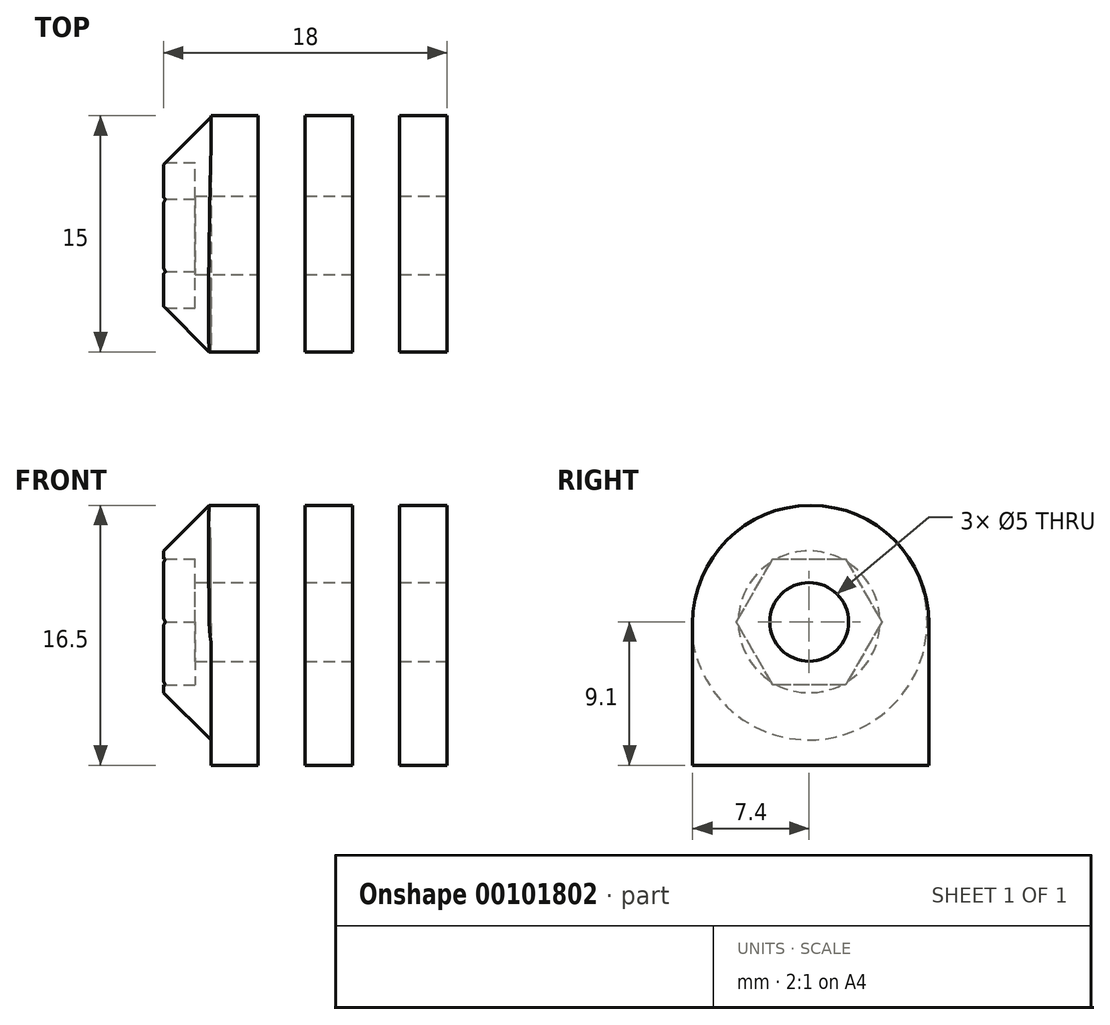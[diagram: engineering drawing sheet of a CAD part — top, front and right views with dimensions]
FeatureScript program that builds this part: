
annotation { "Feature Type Name" : "Feature", "Feature Type Description" : "" }
export const myFeature = defineFeature(function(context is Context, id is Id, definition is map)
    precondition{}
    {
        {
            var Q0;
            Q0=qCreatedBy(makeId("Top.planeOp"),FACE);
            var sketch = newSketch(context, id + "F0", { "sketchPlane" : qUnion([Q0])});
            skLineSegment(sketch, "E0.bottom", {"start": v(0, 15) * mm, "end": v(3, 15) * mm});
            skLineSegment(sketch, "E0.top", {"start": v(0, 0) * mm, "end": v(3, 0) * mm});
            skLineSegment(sketch, "E0.left", {"start": v(0, 15) * mm, "end": v(0, 0) * mm});
            skLineSegment(sketch, "E0.right", {"start": v(3, 15) * mm, "end": v(3, 0) * mm});
            skLineSegment(sketch, "E1.1.0.0", {"start": v(9, 15) * mm, "end": v(9, 0) * mm});
            skLineSegment(sketch, "E1.1.0.1", {"start": v(6, 15) * mm, "end": v(9, 15) * mm});
            skLineSegment(sketch, "E1.1.0.2", {"start": v(6, 15) * mm, "end": v(6, 0) * mm});
            skLineSegment(sketch, "E1.1.0.3", {"start": v(6, 0) * mm, "end": v(9, 0) * mm});
            skLineSegment(sketch, "E1.2.0.0", {"start": v(15, 15) * mm, "end": v(15, 0) * mm});
            skLineSegment(sketch, "E1.2.0.1", {"start": v(12, 15) * mm, "end": v(15, 15) * mm});
            skLineSegment(sketch, "E1.2.0.2", {"start": v(12, 15) * mm, "end": v(12, 0) * mm});
            skLineSegment(sketch, "E1.2.0.3", {"start": v(12, 0) * mm, "end": v(15, 0) * mm});
            skLineSegment(sketch, "E1.direction1", {"start": v(3, 0) * mm, "end": v(9, 0) * mm, "construction": true});
            skSolve(sketch);
        }
        {
            var Q0;
            Q0 = qSketchRegion(id + "F0", true);
            extrude(context, id + "F1", {"entities" : qUnion([Q0]), "depth" : 16.5 * mm});
        }
        {
            var Q0;
            Q0=qCreatedBy(makeId("Right.planeOp"),FACE);
            var sketch = newSketch(context, id + "F2", { "sketchPlane" : qUnion([Q0])});
            skCircle(sketch, "E2", {"center": v(7.4, 9.1) * mm, "radius": 2.5 * mm});
            skCircle(sketch, "E3.cCircle", {"center": v(7.4, 9.1) * mm, "radius": 4 * mm, "construction": true});
            skLineSegment(sketch, "E3.0", {"start": v(5.1, 13.1) * mm, "end": v(9.7, 13.1) * mm});
            skLineSegment(sketch, "E3.1", {"start": v(9.7, 13.1) * mm, "end": v(12.02, 9.1) * mm});
            skLineSegment(sketch, "E3.2", {"start": v(12.02, 9.1) * mm, "end": v(9.7, 5.1) * mm});
            skLineSegment(sketch, "E3.3", {"start": v(9.7, 5.1) * mm, "end": v(5.1, 5.1) * mm});
            skLineSegment(sketch, "E3.4", {"start": v(5.1, 5.1) * mm, "end": v(2.78, 9.1) * mm});
            skLineSegment(sketch, "E3.5", {"start": v(2.78, 9.1) * mm, "end": v(5.1, 13.1) * mm});
            skPoint(sketch, "E3.0.midPoint", {"position": v(7.4, 13.1) * mm});
            skCircle(sketch, "E4", {"center": v(7.4, 9.1) * mm, "radius": 5.5 * mm});
            skSolve(sketch);
        }
        {
            var Q0;
            Q0=makeQuery(id+"F2.imprint","IMPRINT",FACE,{"disambiguationData":[TD([[makeQuery(id+"F2.imprint","IMPRINT",EDGE,{"derivedFrom":sQuery(id+"F2.wireOp",EDGE,"E3.0")}),1.0]])]});
            extrude(context, id + "F3", {"entities" : qUnion([Q0]), "operationType" : NewBodyOperationType.ADD, "oppositeDirection" : true, "depth" : 3 * mm});
        }
        {
            var Q0;
            Q0=makeQuery(id+"F2.imprint","IMPRINT",FACE,{"disambiguationData":[TD([[makeQuery(id+"F2.imprint","IMPRINT",EDGE,{"derivedFrom":sQuery(id+"F2.wireOp",EDGE,"E2")}),1.0]])]});
            extrude(context, id + "F4", {"entities" : qUnion([Q0]), "operationType" : NewBodyOperationType.REMOVE, "oppositeDirection" : true, "depth" : 25 * mm, "hasSecondDirection" : true, "secondDirectionOppositeDirection" : false, "secondDirectionDepth" : 38.1 * mm});
        }
        {
            var Q0;
            Q0=makeQuery(id+"F1.opExtrude","CAP_EDGE",EDGE,{"disambiguationData":[OSD([sQuery(id+"F0.wireOp",EDGE,"E0.bottom")])],"isStart":false});
            var Q1;
            Q1=makeQuery(id+"F1.opExtrude","CAP_EDGE",EDGE,{"disambiguationData":[OSD([sQuery(id+"F0.wireOp",EDGE,"E0.top")])],"isStart":false});
            var Q2;
            Q2=makeQuery(id+"F1.opExtrude","CAP_EDGE",EDGE,{"disambiguationData":[OSD([sQuery(id+"F0.wireOp",EDGE,"E1.1.0.1")])],"isStart":false});
            var Q3;
            Q3=makeQuery(id+"F1.opExtrude","CAP_EDGE",EDGE,{"disambiguationData":[OSD([sQuery(id+"F0.wireOp",EDGE,"E1.1.0.3")])],"isStart":false});
            var Q4;
            Q4=makeQuery(id+"F1.opExtrude","CAP_EDGE",EDGE,{"disambiguationData":[OSD([sQuery(id+"F0.wireOp",EDGE,"E1.2.0.1")])],"isStart":false});
            var Q5;
            Q5=makeQuery(id+"F1.opExtrude","CAP_EDGE",EDGE,{"disambiguationData":[OSD([sQuery(id+"F0.wireOp",EDGE,"E1.2.0.3")])],"isStart":false});
            fillet(context, id + "F5", {"entities" : qUnion([Q0, Q1, Q2, Q3, Q4, Q5]), "radius" : 7.5 * mm, "tangentPropagation" : true, "allowEdgeOverflow" : false});
        }
        {
            var Q0;
            Q0=makeQuery(id+"F3.boolean.opBoolean","SPLIT",FACE,{"disambiguationData":[TD([makeQuery(id+"F3.opExtrude","SWEPT_FACE",FACE,{"disambiguationData":[OSD([sQuery(id+"F2.wireOp",EDGE,"E3.0")])]})])],"derivedFrom":makeQuery(id+"F1.opExtrude","SWEPT_FACE",FACE,{"disambiguationData":[OSD([sQuery(id+"F0.wireOp",EDGE,"E0.left")])]})});
            extrude(context, id + "F6", {"entities" : qUnion([Q0]), "operationType" : NewBodyOperationType.ADD, "depth" : 1 * mm});
        }
        {
            var Q0;
            Q0=makeQuery(id+"F3.opExtrude","CAP_EDGE",EDGE,{"disambiguationData":[OSD([sQuery(id+"F2.wireOp",EDGE,"E4")])],"isStart":true});
            chamfer(context, id + "F7", {"entities" : qUnion([Q0]), "width" : 2 * mm, "tangentPropagation" : true});
        }
        {
            var Q0;
            Q0=makeQuery(id+"F3.opExtrude","CAP_EDGE",EDGE,{"disambiguationData":[OSD([sQuery(id+"F2.wireOp",EDGE,"E4")])],"isStart":false});
            chamfer(context, id + "F8", {"entities" : qUnion([Q0]), "width" : 1 * mm, "tangentPropagation" : true});
        }
    });
